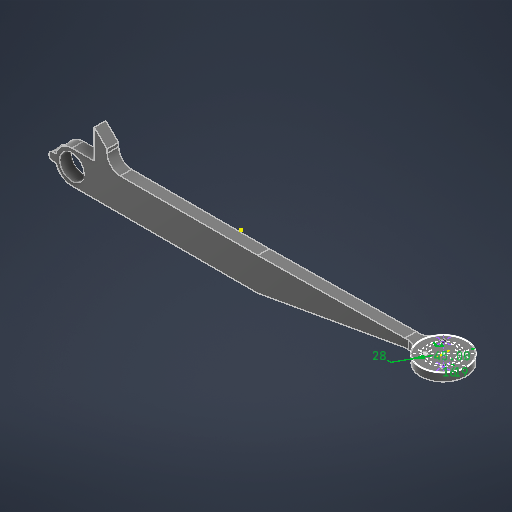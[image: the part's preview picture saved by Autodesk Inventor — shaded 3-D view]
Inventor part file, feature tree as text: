
AUTODESK INVENTOR PART (.ipt)
format: ipt  version: 2025 (Build 290162010, 162A)  size: 294,400 bytes
history: native  units: mm
features: extrude x3, sketch x3, fillet x2, hole x1
ambient origin geometry x8: Origin, YZ Plane, XZ Plane, XY Plane, X Axis, Y Axis, Z Axis, Center Point
bodies: Solid1 (feature_tree)
feature tree (9):
  extrude  "Extrusion1"  Depth=20.0mm
  sketch  "Sketch2"  dims[d2=203.2mm d3=20.0mm]
  extrude  "Extrusion2"  Depth=20.0mm
  hole  "Hole1"  [1 undecoded]
  fillet  "Fillet1"  Radius=28.0mm
  extrude  "Extrusion4"  Depth=2.0mm
  fillet  "Fillet3"  Radius=16.0mm
  sketch  "Sketch1"  dims[d0=20.0mm d1=15.0mm]
  sketch  "Sketch4"  dims[d4=5.0mm d5=7.0mm d6=0.0mm d7=28.0mm d8=19.0mm d9=16.0mm d10=45.0deg d11=5.0mm d12=0.0mm d13=3.0mm d14=6.0mm d15=4.0mm d16=2.0mm d17=90.0deg d18=4.0mm d19=0.0mm d23=6.0mm d37=10.0mm d38=0.0mm d39=8.0mm d42=8.0mm d43=2.0mm d41=0.5mm d44=0.872665mm]
note: 1 required parameter value undecoded (feature->parameter linkage not recoverable at this tier; creation-order binding heuristic only, values carry confidence <= 0.55)
